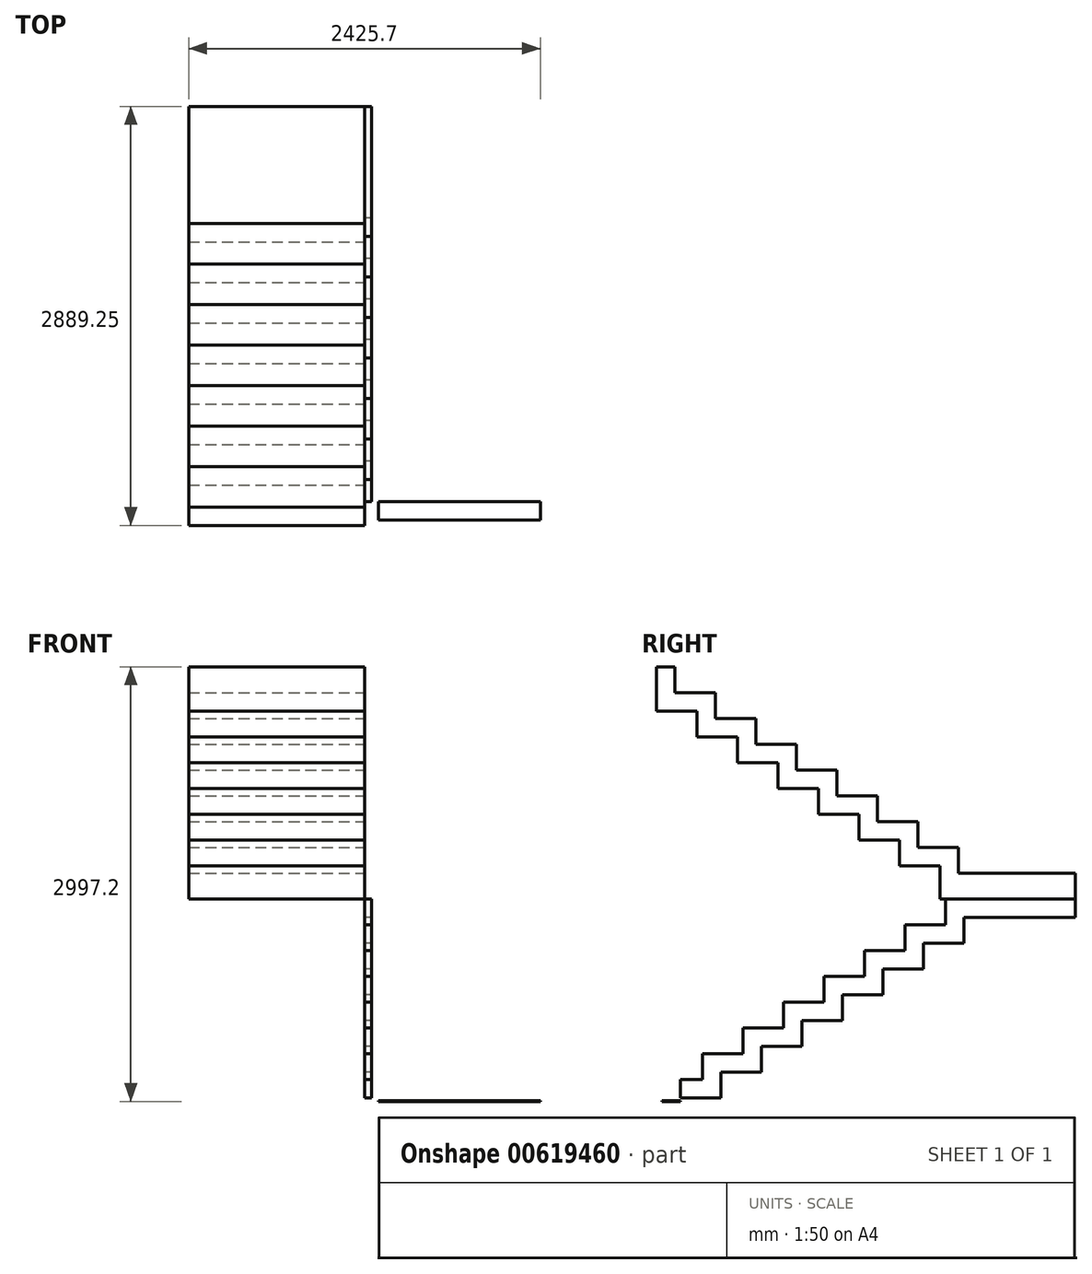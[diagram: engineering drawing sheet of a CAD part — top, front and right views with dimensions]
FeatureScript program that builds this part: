
annotation { "Feature Type Name" : "Feature", "Feature Type Description" : "" }
export const myFeature = defineFeature(function(context is Context, id is Id, definition is map)
    precondition{}
    {
        {
            assignVariable(context, id + "F0", {"name" : "a", "anyValue" : 44});
        }
        {
            assignVariable(context, id + "F1", {"name" : "tk2", "anyValue" : 1});
        }
        {
            var Q0;
            Q0=qCreatedBy(makeId("Top.planeOp"),FACE);
            var sketch = newSketch(context, id + "F2", { "sketchPlane" : qUnion([Q0])});
            skLineSegment(sketch, "E0.bottom", {"start": v(-1212.85, 914.4) * mm, "end": v(1212.85, 914.4) * mm});
            skLineSegment(sketch, "E0.top", {"start": v(-1212.85, 0) * mm, "end": v(1212.85, 0) * mm});
            skLineSegment(sketch, "E0.left", {"start": v(-1212.85, 914.4) * mm, "end": v(-1212.85, 0) * mm});
            skLineSegment(sketch, "E0.right", {"start": v(1212.85, 914.4) * mm, "end": v(1212.85, 0) * mm});
            skLineSegment(sketch, "E1", {"start": v(-1212.85, 0) * mm, "end": v(-1212.85, -279.4) * mm});
            skLineSegment(sketch, "E2", {"start": v(-1212.85, -279.4) * mm, "end": v(-95.25, -279.4) * mm});
            skLineSegment(sketch, "E3", {"start": v(-95.25, -279.4) * mm, "end": v(-95.25, 0) * mm});
            skLineSegment(sketch, "E4", {"start": v(1212.85, 0) * mm, "end": v(1212.85, -279.4) * mm});
            skLineSegment(sketch, "E5", {"start": v(1212.85, -279.4) * mm, "end": v(95.25, -279.4) * mm});
            skLineSegment(sketch, "E6", {"start": v(95.25, -279.4) * mm, "end": v(95.25, 0) * mm});
            skLineSegment(sketch, "E7", {"start": v(95.25, -279.4) * mm, "end": v(95.25, -558.8) * mm});
            skLineSegment(sketch, "E8", {"start": v(95.25, -558.8) * mm, "end": v(1212.85, -558.8) * mm});
            skLineSegment(sketch, "E9", {"start": v(1212.85, -558.8) * mm, "end": v(1212.85, -279.4) * mm});
            skLineSegment(sketch, "E10", {"start": v(95.25, -558.8) * mm, "end": v(95.25, -838.2) * mm});
            skLineSegment(sketch, "E11", {"start": v(95.25, -838.2) * mm, "end": v(1212.85, -838.2) * mm});
            skLineSegment(sketch, "E12", {"start": v(1212.85, -838.2) * mm, "end": v(1212.85, -558.8) * mm});
            skLineSegment(sketch, "E13", {"start": v(95.25, -838.2) * mm, "end": v(95.25, -1117.6) * mm});
            skLineSegment(sketch, "E14", {"start": v(95.25, -1117.6) * mm, "end": v(1212.85, -1117.6) * mm});
            skLineSegment(sketch, "E15", {"start": v(1212.85, -1117.6) * mm, "end": v(1212.85, -838.2) * mm});
            skLineSegment(sketch, "E16", {"start": v(95.25, -1117.6) * mm, "end": v(95.25, -1397) * mm});
            skLineSegment(sketch, "E17", {"start": v(95.25, -1397) * mm, "end": v(1212.85, -1397) * mm});
            skLineSegment(sketch, "E18", {"start": v(1212.85, -1397) * mm, "end": v(1212.85, -1117.6) * mm});
            skLineSegment(sketch, "E19", {"start": v(95.25, -1397) * mm, "end": v(95.25, -1676.4) * mm});
            skLineSegment(sketch, "E20", {"start": v(95.25, -1676.4) * mm, "end": v(1212.85, -1676.4) * mm});
            skLineSegment(sketch, "E21", {"start": v(1212.85, -1676.4) * mm, "end": v(1212.85, -1397) * mm});
            skLineSegment(sketch, "E22", {"start": v(95.25, -1676.4) * mm, "end": v(95.25, -1955.8) * mm});
            skLineSegment(sketch, "E23", {"start": v(95.25, -1955.8) * mm, "end": v(1212.85, -1955.8) * mm});
            skLineSegment(sketch, "E24", {"start": v(1212.85, -1955.8) * mm, "end": v(1212.85, -1676.4) * mm});
            skLineSegment(sketch, "E25", {"start": v(0, 0) * mm, "end": v(0, 914.4) * mm});
            skLineSegment(sketch, "E26", {"start": v(95.25, -1936.75) * mm, "end": v(1212.85, -1936.75) * mm});
            skLineSegment(sketch, "E27", {"start": v(95.25, -1809.75) * mm, "end": v(1212.85, -1809.75) * mm});
            skSolve(sketch);
        }
        {
            var Q0;
            {var subQ0=sQuery(id+"F2.wireOp",EDGE,"E26");Q0=makeQuery(id+"F2.imprint","IMPRINT",FACE,{"disambiguationData":[TD([[makeQuery(id+"F2.imprint","IMPRINT",EDGE,{"derivedFrom":subQ0}),1.0]])]});}
            extrude(context, id + "F3", {"entities" : qUnion([Q0]), "depth" : (7 - getVariable(context, 'tk2')) * mm, "offsetDistance" : 25.4 * mm});
        }
        {
            var Q0;
            Q0=qCreatedBy(makeId("Right.planeOp"),FACE);
            var sketch = newSketch(context, id + "F4", { "sketchPlane" : qUnion([Q0])});
            skLineSegment(sketch, "E28", {"start": v(-1955.8, 177.8) * mm, "end": v(-1955.8, 0) * mm, "construction": true});
            skLineSegment(sketch, "E29", {"start": v(-1955.8, 177.8) * mm, "end": v(-1676.4, 177.8) * mm, "construction": true});
            skLineSegment(sketch, "E30", {"start": v(-1676.4, 177.8) * mm, "end": v(-1676.4, 355.6) * mm, "construction": true});
            skLineSegment(sketch, "E31", {"start": v(-1809.75, 152.4) * mm, "end": v(-1657.35, 152.4) * mm});
            skLineSegment(sketch, "E32", {"start": v(-1657.35, 152.4) * mm, "end": v(-1657.35, 330.2) * mm});
            skLineSegment(sketch, "E33", {"start": v(-1657.35, 330.2) * mm, "end": v(-1377.95, 330.2) * mm});
            skLineSegment(sketch, "E34", {"start": v(-1377.95, 330.2) * mm, "end": v(-1377.95, 508) * mm});
            skLineSegment(sketch, "E35", {"start": v(-1377.95, 508) * mm, "end": v(-1098.55, 508) * mm});
            skLineSegment(sketch, "E36", {"start": v(-1098.55, 508) * mm, "end": v(-1098.55, 685.8) * mm});
            skLineSegment(sketch, "E37", {"start": v(-1098.55, 685.8) * mm, "end": v(-819.15, 685.8) * mm});
            skLineSegment(sketch, "E38", {"start": v(-819.15, 685.8) * mm, "end": v(-819.15, 863.6) * mm});
            skLineSegment(sketch, "E39", {"start": v(-819.15, 863.6) * mm, "end": v(-539.75, 863.6) * mm});
            skLineSegment(sketch, "E40", {"start": v(-539.75, 863.6) * mm, "end": v(-539.75, 1041.4) * mm});
            skLineSegment(sketch, "E41", {"start": v(-539.75, 1041.4) * mm, "end": v(-260.35, 1041.4) * mm});
            skLineSegment(sketch, "E42", {"start": v(-260.35, 1041.4) * mm, "end": v(-260.35, 1219.2) * mm});
            skLineSegment(sketch, "E43", {"start": v(-260.35, 1219.2) * mm, "end": v(19.05, 1219.2) * mm});
            skLineSegment(sketch, "E44", {"start": v(146.05, 1092.2) * mm, "end": v(-133.35, 1092.2) * mm});
            skLineSegment(sketch, "E45", {"start": v(-133.35, 1092.2) * mm, "end": v(-133.35, 914.4) * mm});
            skLineSegment(sketch, "E46", {"start": v(-133.35, 914.4) * mm, "end": v(-412.75, 914.4) * mm});
            skLineSegment(sketch, "E47", {"start": v(-412.75, 914.4) * mm, "end": v(-412.75, 736.6) * mm});
            skLineSegment(sketch, "E48", {"start": v(-412.75, 736.6) * mm, "end": v(-692.15, 736.6) * mm});
            skLineSegment(sketch, "E49", {"start": v(-692.15, 736.6) * mm, "end": v(-692.15, 558.8) * mm});
            skLineSegment(sketch, "E50", {"start": v(-692.15, 558.8) * mm, "end": v(-971.55, 558.8) * mm});
            skLineSegment(sketch, "E51", {"start": v(-971.55, 558.8) * mm, "end": v(-971.55, 381) * mm});
            skLineSegment(sketch, "E52", {"start": v(-971.55, 381) * mm, "end": v(-1250.95, 381) * mm});
            skLineSegment(sketch, "E53", {"start": v(-1250.95, 381) * mm, "end": v(-1250.95, 203.2) * mm});
            skLineSegment(sketch, "E54", {"start": v(-1250.95, 203.2) * mm, "end": v(-1530.35, 203.2) * mm});
            skLineSegment(sketch, "E55", {"start": v(-1530.35, 203.2) * mm, "end": v(-1530.35, 25.4) * mm});
            skLineSegment(sketch, "E56", {"start": v(-1530.35, 25.4) * mm, "end": v(-1809.75, 25.4) * mm});
            skLineSegment(sketch, "E57", {"start": v(-1809.75, 25.4) * mm, "end": v(-1809.75, 152.4) * mm});
            skLineSegment(sketch, "E58", {"start": v(19.05, 1219.2) * mm, "end": v(19.05, 1397) * mm});
            skLineSegment(sketch, "E59", {"start": v(19.05, 1397) * mm, "end": v(914.4, 1397) * mm});
            skLineSegment(sketch, "E60", {"start": v(914.4, 1397) * mm, "end": v(914.4, 1270) * mm});
            skLineSegment(sketch, "E61", {"start": v(914.4, 1270) * mm, "end": v(146.05, 1270) * mm});
            skLineSegment(sketch, "E62", {"start": v(146.05, 1270) * mm, "end": v(146.05, 1092.2) * mm});
            skSolve(sketch);
        }
        {
            var Q0;
            Q0=makeQuery(id+"F4.imprint","IMPRINT",FACE,{"disambiguationData":[TD([[makeQuery(id+"F4.imprint","IMPRINT",EDGE,{"derivedFrom":sQuery(id+"F4.wireOp",EDGE,"E31")}),-1.0]])]});
            extrude(context, id + "F5", {"entities" : qUnion([Q0]), "operationType" : NewBodyOperationType.ADD, "depth" : (getVariable(context, 'a') + 3.75) * mm, "offsetDistance" : 25.4 * mm});
        }
        {
            var Q0;
            Q0=qCreatedBy(makeId("Right.planeOp"),FACE);
            var sketch = newSketch(context, id + "F6", { "sketchPlane" : qUnion([Q0])});
            skLineSegment(sketch, "E63", {"start": v(914.4, 1397) * mm, "end": v(-19.05, 1397) * mm});
            skLineSegment(sketch, "E64", {"start": v(-19.05, 1397) * mm, "end": v(-19.05, 1625.6) * mm});
            skLineSegment(sketch, "E65", {"start": v(-19.05, 1625.6) * mm, "end": v(-298.45, 1625.6) * mm});
            skLineSegment(sketch, "E66", {"start": v(-298.45, 1625.6) * mm, "end": v(-298.45, 1803.4) * mm});
            skLineSegment(sketch, "E67", {"start": v(-298.45, 1803.4) * mm, "end": v(-577.85, 1803.4) * mm});
            skLineSegment(sketch, "E68", {"start": v(-577.85, 1803.4) * mm, "end": v(-577.85, 1981.2) * mm});
            skLineSegment(sketch, "E69", {"start": v(-577.85, 1981.2) * mm, "end": v(-857.25, 1981.2) * mm});
            skLineSegment(sketch, "E70", {"start": v(-857.25, 1981.2) * mm, "end": v(-857.25, 2159) * mm});
            skLineSegment(sketch, "E71", {"start": v(-857.25, 2159) * mm, "end": v(-1136.65, 2159) * mm});
            skLineSegment(sketch, "E72", {"start": v(-1136.65, 2159) * mm, "end": v(-1136.65, 2336.8) * mm});
            skLineSegment(sketch, "E73", {"start": v(-1136.65, 2336.8) * mm, "end": v(-1416.05, 2336.8) * mm});
            skLineSegment(sketch, "E74", {"start": v(-1416.05, 2336.8) * mm, "end": v(-1416.05, 2514.6) * mm});
            skLineSegment(sketch, "E75", {"start": v(-1695.45, 2692.4) * mm, "end": v(-1974.85, 2692.4) * mm});
            skLineSegment(sketch, "E76", {"start": v(-1974.85, 2692.4) * mm, "end": v(-1974.85, 2997.2) * mm});
            skLineSegment(sketch, "E77", {"start": v(-1974.85, 2997.2) * mm, "end": v(-1847.85, 2997.2) * mm});
            skLineSegment(sketch, "E78", {"start": v(-1847.85, 2997.2) * mm, "end": v(-1847.85, 2819.4) * mm});
            skLineSegment(sketch, "E79", {"start": v(-1847.85, 2819.4) * mm, "end": v(-1568.45, 2819.4) * mm});
            skLineSegment(sketch, "E80", {"start": v(-1568.45, 2819.4) * mm, "end": v(-1568.45, 2641.6) * mm});
            skLineSegment(sketch, "E81", {"start": v(-1568.45, 2641.6) * mm, "end": v(-1289.05, 2641.6) * mm});
            skLineSegment(sketch, "E82", {"start": v(-1289.05, 2641.6) * mm, "end": v(-1289.05, 2463.8) * mm});
            skLineSegment(sketch, "E83", {"start": v(-1289.05, 2463.8) * mm, "end": v(-1009.65, 2463.8) * mm});
            skLineSegment(sketch, "E84", {"start": v(-1009.65, 2463.8) * mm, "end": v(-1009.65, 2286) * mm});
            skLineSegment(sketch, "E85", {"start": v(-1009.65, 2286) * mm, "end": v(-730.25, 2286) * mm});
            skLineSegment(sketch, "E86", {"start": v(-730.25, 2286) * mm, "end": v(-730.25, 2108.2) * mm});
            skLineSegment(sketch, "E87", {"start": v(-730.25, 2108.2) * mm, "end": v(-450.85, 2108.2) * mm});
            skLineSegment(sketch, "E88", {"start": v(-450.85, 2108.2) * mm, "end": v(-450.85, 1930.4) * mm});
            skLineSegment(sketch, "E89", {"start": v(-450.85, 1930.4) * mm, "end": v(-171.45, 1930.4) * mm});
            skLineSegment(sketch, "E90", {"start": v(-171.45, 1930.4) * mm, "end": v(-171.45, 1752.6) * mm});
            skLineSegment(sketch, "E91", {"start": v(-171.45, 1752.6) * mm, "end": v(107.95, 1752.6) * mm});
            skLineSegment(sketch, "E92", {"start": v(107.95, 1752.6) * mm, "end": v(107.95, 1574.8) * mm});
            skLineSegment(sketch, "E93", {"start": v(107.95, 1574.8) * mm, "end": v(914.4, 1574.8) * mm});
            skLineSegment(sketch, "E94", {"start": v(914.4, 1574.8) * mm, "end": v(914.4, 1397) * mm});
            skLineSegment(sketch, "E95", {"start": v(-1416.05, 2514.6) * mm, "end": v(-1695.45, 2514.6) * mm});
            skLineSegment(sketch, "E96", {"start": v(-1695.45, 2514.6) * mm, "end": v(-1695.45, 2692.4) * mm});
            skSolve(sketch);
        }
        {
            var Q0;
            Q0=makeQuery(id+"F6.imprint","IMPRINT",FACE,{"disambiguationData":[TD([[makeQuery(id+"F6.imprint","IMPRINT",EDGE,{"derivedFrom":sQuery(id+"F6.wireOp",EDGE,"E63")}),-1.0]])]});
            extrude(context, id + "F7", {"entities" : qUnion([Q0]), "oppositeDirection" : true, "depth" : 1212.85 * mm, "offsetDistance" : 25.4 * mm});
        }
    });
